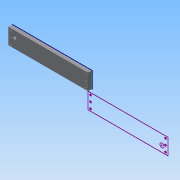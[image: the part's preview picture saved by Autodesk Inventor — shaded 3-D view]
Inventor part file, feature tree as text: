
AUTODESK INVENTOR PART (.ipt)
format: ipt  version: 2015 (Build 190159000, 159)  size: 112,640 bytes
history: native  units: mm
features: other x5, extrude x1, sketch x1, projected_geometry x1
ambient origin geometry x8: Origin, YZ Plane, XZ Plane, XY Plane, X Axis, Y Axis, Z Axis, Center Point
bodies: Body1 (feature_tree)
feature tree (8):
  other  "Blocks"
  extrude  "Extrusion3"  Depth=40.0mm
  sketch  "Sketch2"  dims[d0=200.0mm d1=40.0mm d4=4.0mm d5=4.0mm d6=5.0mm d7=5.0mm d8=4.0mm d9=20.0mm d10=100.0mm d13=10.0mm d14=15.0mm d15=15.0mm d16=10.0mm d17=0.0mm]
  other  "DXF"
  projected_geometry  "Projected Loop1"
  other  "Block1"
  other  "Block1:1"
  other  "Block1:2"
